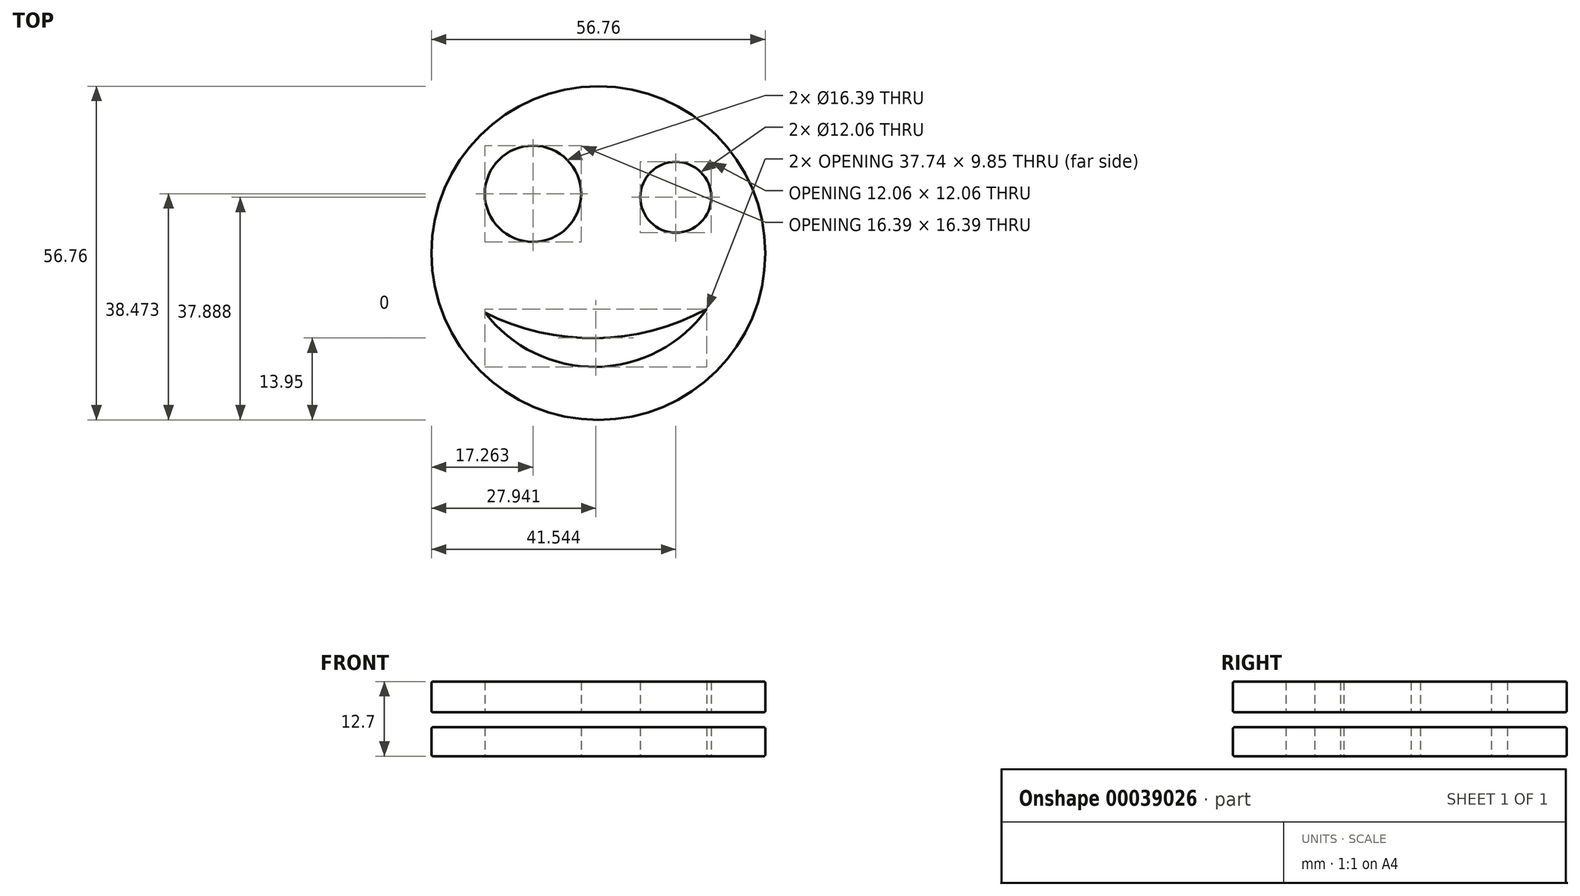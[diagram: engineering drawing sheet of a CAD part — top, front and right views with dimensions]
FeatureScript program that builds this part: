
annotation { "Feature Type Name" : "Feature", "Feature Type Description" : "" }
export const myFeature = defineFeature(function(context is Context, id is Id, definition is map)
    precondition{}
    {
        {
            var Q0;
            Q0=qCreatedBy(makeId("Top.planeOp"),FACE);
            var sketch = newSketch(context, id + "F0", { "sketchPlane" : qUnion([Q0])});
            skCircle(sketch, "E0", {"center": v(0, 0) * mm, "radius": 28.38 * mm});
            skCircle(sketch, "E1", {"center": v(-11.12, 10.1) * mm, "radius": 8.2 * mm});
            skCircle(sketch, "E2", {"center": v(13.16, 9.5) * mm, "radius": 6.03 * mm});
            skArc(sketch, "E3", {"start": v(-19.3, -10.1) * mm, "mid": v(-0.3, -19.35) * mm, "end": v(18.43, -9.5) * mm});
            skArc(sketch, "E4", {"start": v(-19.3, -10.1) * mm, "mid": v(-0.37, -14.48) * mm, "end": v(18.43, -9.5) * mm});
            skSolve(sketch);
        }
        {
            var Q0;
            Q0 = qSketchRegion(id + "F0", true);
            var Q1;
            Q1=makeQuery(id+"F0.imprint","IMPRINT",FACE,{"disambiguationData":[TD([[makeQuery(id+"F0.imprint","IMPRINT",EDGE,{"derivedFrom":sQuery(id+"F0.wireOp",EDGE,"E0")}),1.0]])]});
            extrude(context, id + "F1", {"entities" : qUnion([Q0, Q1]), "depth" : 12.7 * mm});
        }
        {
            var Q0;
            Q0=qCreatedBy(makeId("Front.planeOp"),FACE);
            var sketch = newSketch(context, id + "F2", { "sketchPlane" : qUnion([Q0])});
            skLineSegment(sketch, "E5.bottom", {"start": v(-54.12, 7.44) * mm, "end": v(56.37, 7.44) * mm});
            skLineSegment(sketch, "E5.top", {"start": v(-54.12, 4.9) * mm, "end": v(56.37, 4.9) * mm});
            skLineSegment(sketch, "E5.left", {"start": v(-54.12, 7.44) * mm, "end": v(-54.12, 4.9) * mm});
            skLineSegment(sketch, "E5.right", {"start": v(56.37, 7.44) * mm, "end": v(56.37, 4.9) * mm});
            skSolve(sketch);
        }
        {
            var Q0;
            Q0 = qSketchRegion(id + "F2", true);
            extrude(context, id + "F3", {"entities" : qUnion([Q0]), "operationType" : NewBodyOperationType.REMOVE, "endBound" : BoundingType.SYMMETRIC, "oppositeDirection" : true, "depth" : 79.93 * mm});
        }
        {
            var Q0;
            Q0=makeQuery(id+"F1.opExtrude","CAP_EDGE",EDGE,{"disambiguationData":[OSD([sQuery(id+"F0.wireOp",EDGE,"E0")])],"isStart":false});
            var Q1;
            Q1=makeQuery(id+"F1.opExtrude","CAP_EDGE",EDGE,{"disambiguationData":[OSD([sQuery(id+"F0.wireOp",EDGE,"E0")])],"isStart":true});
            var Q2;
            Q2=makeQuery(id+"F3.boolean.opBoolean","INTERSECT",EDGE,{"derivedFrom":[makeQuery(id+"F1.opExtrude","SWEPT_FACE",FACE,{"disambiguationData":[OSD([sQuery(id+"F0.wireOp",EDGE,"E0")])]}),makeQuery(id+"F3.opExtrude","SWEPT_FACE",FACE,{"disambiguationData":[OSD([sQuery(id+"F2.wireOp",EDGE,"E5.bottom")])]})]});
            var Q3;
            Q3=makeQuery(id+"F3.boolean.opBoolean","INTERSECT",EDGE,{"derivedFrom":[makeQuery(id+"F1.opExtrude","SWEPT_FACE",FACE,{"disambiguationData":[OSD([sQuery(id+"F0.wireOp",EDGE,"E0")])]}),makeQuery(id+"F3.opExtrude","SWEPT_FACE",FACE,{"disambiguationData":[OSD([sQuery(id+"F2.wireOp",EDGE,"E5.top")])]})]});
            fillet(context, id + "F4", {"entities" : qUnion([Q0, Q1, Q2, Q3]), "radius" : 0.25 * mm, "tangentPropagation" : true, "allowEdgeOverflow" : false});
        }
    });
